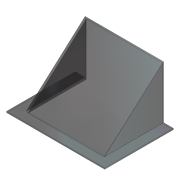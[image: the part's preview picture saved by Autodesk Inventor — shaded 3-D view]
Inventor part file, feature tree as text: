
AUTODESK INVENTOR PART (.ipt)
format: ipt  version: 2012 (Build 160160000, 160)  size: 105,472 bytes
history: native  units: in
note: dims shown in document units (in); Inventor stores cm internally (conversion verified against a paired STEP export)
features: extrude x3, sketch x3, shell x1
ambient origin geometry x8: Origin, YZ Plane, XZ Plane, XY Plane, X Axis, Y Axis, Z Axis, Center Point
bodies: Solid1 (feature_tree)
feature tree (7):
  extrude  "Extrusion1"  Depth=5.5in
  extrude  "Extrusion3"  Depth=0.125in
  extrude  "Extrusion4"  Depth=6.0in TaperAngle=0.0deg
  shell  "Shell1"  Thickness=0.125in
  sketch  "Sketch1"  dims[d0=10.0in d1=5.5in]
  sketch  "Sketch4"  dims[d2=7.0in d3=0.0in d10=0.125in]
  sketch  "Sketch5"  dims[d11=1.0in d12=6.0in d13=0.0in d15=0.125in d16=1.0in d17=6.0in d18=0.0in d19=0.125in]
